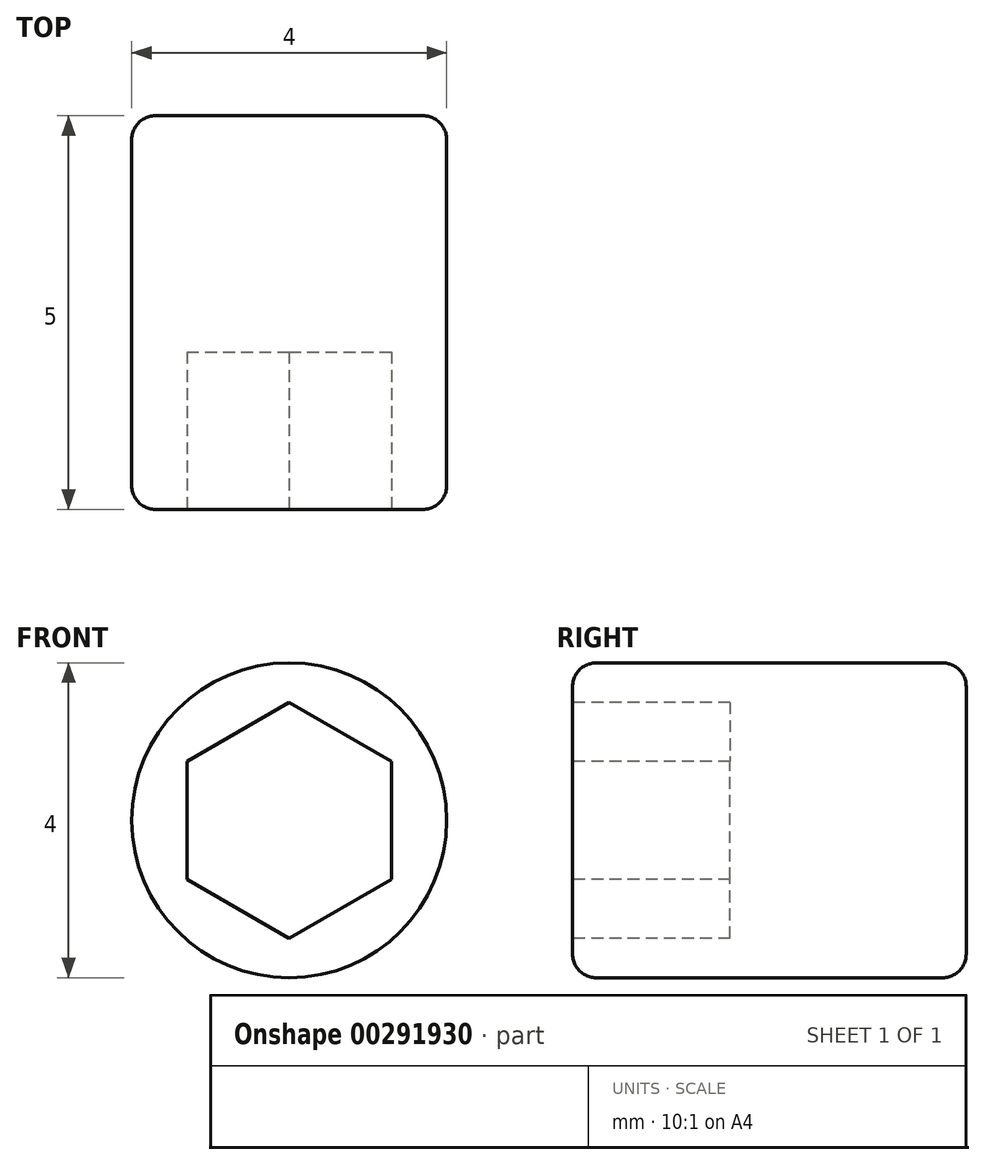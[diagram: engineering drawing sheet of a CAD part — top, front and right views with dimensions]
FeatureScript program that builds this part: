
annotation { "Feature Type Name" : "Feature", "Feature Type Description" : "" }
export const myFeature = defineFeature(function(context is Context, id is Id, definition is map)
    precondition{}
    {
        {
            var Q0;
            Q0=qCreatedBy(makeId("Front.planeOp"),FACE);
            var sketch = newSketch(context, id + "F0", { "sketchPlane" : qUnion([Q0])});
            skCircle(sketch, "E0", {"center": v(0, 0) * mm, "radius": 2 * mm});
            skSolve(sketch);
        }
        {
            var Q0;
            Q0=makeQuery(id+"F0.imprint","IMPRINT",FACE,{"disambiguationData":[TD([[makeQuery(id+"F0.imprint","IMPRINT",EDGE,{"derivedFrom":sQuery(id+"F0.wireOp",EDGE,"E0")}),1.0]])]});
            extrude(context, id + "F1", {"entities" : qUnion([Q0]), "oppositeDirection" : true, "depth" : 5 * mm});
        }
        {
            var Q0;
            Q0=makeQuery(id+"F1.opExtrude","CAP_FACE",FACE,{"disambiguationData":[OSD([sQuery(id+"F0.wireOp",EDGE,"E0")])],"isStart":true});
            var sketch = newSketch(context, id + "F2", { "sketchPlane" : qUnion([Q0])});
            skCircle(sketch, "E1.cCircle", {"center": v(0, 0) * mm, "radius": 1.5 * mm, "construction": true});
            skLineSegment(sketch, "E1.0", {"start": v(0, 1.5) * mm, "end": v(1.3, 0.75) * mm});
            skLineSegment(sketch, "E1.1", {"start": v(1.3, 0.75) * mm, "end": v(1.3, -0.75) * mm});
            skLineSegment(sketch, "E1.2", {"start": v(1.3, -0.75) * mm, "end": v(0, -1.5) * mm});
            skLineSegment(sketch, "E1.3", {"start": v(0, -1.5) * mm, "end": v(-1.3, -0.75) * mm});
            skLineSegment(sketch, "E1.4", {"start": v(-1.3, -0.75) * mm, "end": v(-1.3, 0.75) * mm});
            skLineSegment(sketch, "E1.5", {"start": v(-1.3, 0.75) * mm, "end": v(0, 1.5) * mm});
            skSolve(sketch);
        }
        {
            var Q0;
            Q0=makeQuery(id+"F2.imprint","IMPRINT",FACE,{"disambiguationData":[TD([[makeQuery(id+"F2.imprint","IMPRINT",EDGE,{"derivedFrom":sQuery(id+"F2.wireOp",EDGE,"E1.0")}),-1.0]])]});
            extrude(context, id + "F3", {"entities" : qUnion([Q0]), "operationType" : NewBodyOperationType.REMOVE, "oppositeDirection" : true, "depth" : 2 * mm});
        }
        {
            var Q0;
            Q0=makeQuery(id+"F1.opExtrude","CAP_EDGE",EDGE,{"disambiguationData":[OSD([sQuery(id+"F0.wireOp",EDGE,"E0")])],"isStart":true});
            var Q1;
            Q1=makeQuery(id+"F1.opExtrude","CAP_EDGE",EDGE,{"disambiguationData":[OSD([sQuery(id+"F0.wireOp",EDGE,"E0")])],"isStart":false});
            fillet(context, id + "F4", {"entities" : qUnion([Q0, Q1]), "radius" : 0.3 * mm, "tangentPropagation" : true, "allowEdgeOverflow" : false});
        }
    });
